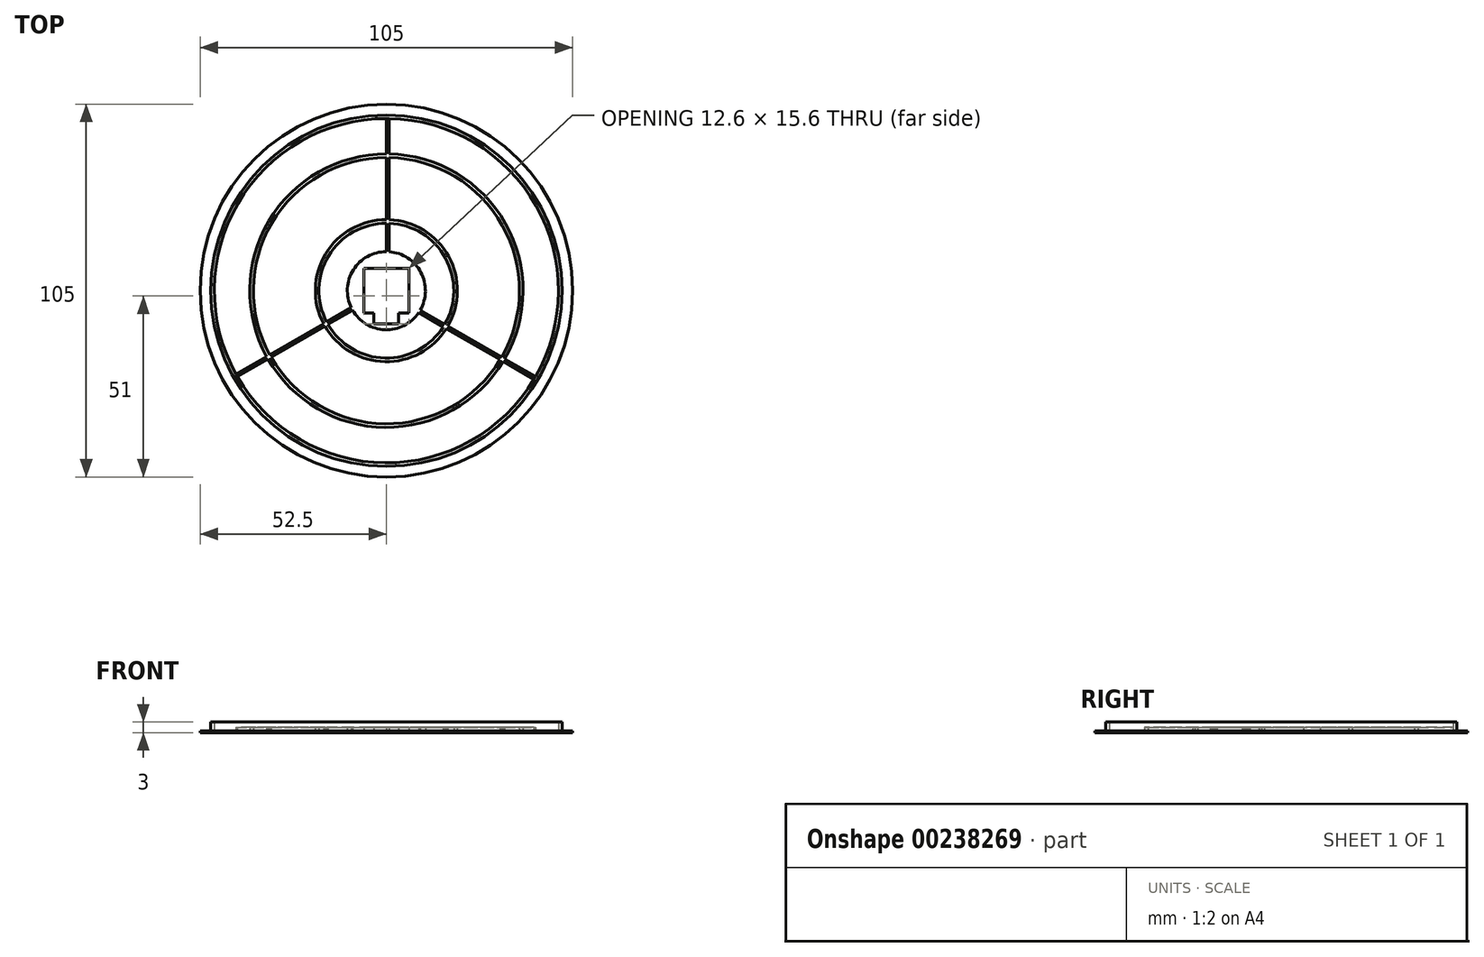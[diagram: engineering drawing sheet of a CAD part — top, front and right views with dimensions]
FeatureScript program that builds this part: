
annotation { "Feature Type Name" : "Feature", "Feature Type Description" : "" }
export const myFeature = defineFeature(function(context is Context, id is Id, definition is map)
    precondition{}
    {
        {
            var Q0;
            Q0=qCreatedBy(makeId("Top.planeOp"),FACE);
            var sketch = newSketch(context, id + "F0", { "sketchPlane" : qUnion([Q0])});
            skLineSegment(sketch, "E0.bottom", {"start": v(6.3, -6.3) * mm, "end": v(-6.3, -6.3) * mm});
            skLineSegment(sketch, "E0.top", {"start": v(6.3, 6.3) * mm, "end": v(-6.3, 6.3) * mm});
            skLineSegment(sketch, "E0.left", {"start": v(6.3, -6.3) * mm, "end": v(6.3, 6.3) * mm});
            skLineSegment(sketch, "E0.right", {"start": v(-6.3, -6.3) * mm, "end": v(-6.3, 6.3) * mm});
            skPoint(sketch, "E0.middle", {"position": v(0, 0) * mm});
            skCircle(sketch, "E1", {"center": v(0, 0) * mm, "radius": 11 * mm});
            skCircle(sketch, "E2", {"center": v(0, 0) * mm, "radius": 52.5 * mm});
            skLineSegment(sketch, "E3.bottom", {"start": v(3.5, -9.3) * mm, "end": v(-3.5, -9.3) * mm});
            skLineSegment(sketch, "E3.top", {"start": v(3.5, -6.3) * mm, "end": v(-3.5, -6.3) * mm});
            skLineSegment(sketch, "E3.left", {"start": v(3.5, -9.3) * mm, "end": v(3.5, -6.3) * mm});
            skLineSegment(sketch, "E3.right", {"start": v(-3.5, -9.3) * mm, "end": v(-3.5, -6.3) * mm});
            skPoint(sketch, "E3.middle", {"position": v(0, -7.8) * mm});
            skPoint(sketch, "E3.middle.positionSnap0", {"position": v(0, -6.3) * mm});
            skPoint(sketch, "E3.centerSnap0", {"position": v(0, -6.3) * mm});
            skCircle(sketch, "E4", {"center": v(0, 0) * mm, "radius": 49.5 * mm});
            skArc(sketch, "E5", {"start": v(0, 48.5) * mm, "mid": v(-41.8, 24.6) * mm, "end": v(-42.4, -23.56) * mm});
            skArc(sketch, "E6", {"start": v(-33.34, -19.25) * mm, "mid": v(-0.4, -38.5) * mm, "end": v(32.94, -19.93) * mm});
            skArc(sketch, "E7", {"start": v(-32.48, -18.75) * mm, "mid": v(-0.4, -37.5) * mm, "end": v(32.07, -19.43) * mm});
            skArc(sketch, "E8", {"start": v(-16.45, -9.5) * mm, "mid": v(-0.4, -19) * mm, "end": v(16.05, -10.18) * mm});
            skArc(sketch, "E9", {"start": v(-17.32, -10) * mm, "mid": v(-0.4, -20) * mm, "end": v(16.91, -10.68) * mm});
            skLineSegment(sketch, "E10", {"start": v(0, 11) * mm, "end": v(0, 19) * mm});
            skLineSegment(sketch, "E11", {"start": v(0.79, 48.5) * mm, "end": v(0.79, 38.5) * mm});
            skLineSegment(sketch, "E12.1.0", {"start": v(-9.53, -5.5) * mm, "end": v(-16.45, -9.5) * mm});
            skLineSegment(sketch, "E12.1.1", {"start": v(-42.4, -23.56) * mm, "end": v(-33.73, -18.56) * mm});
            skLineSegment(sketch, "E12.2.0", {"start": v(9.53, -5.5) * mm, "end": v(16.45, -9.5) * mm});
            skLineSegment(sketch, "E12.2.1", {"start": v(41.6, -24.93) * mm, "end": v(32.94, -19.93) * mm});
            skLineSegment(sketch, "E13.trimOffspring", {"start": v(-32.86, -18.06) * mm, "end": v(-17.7, -9.3) * mm});
            skLineSegment(sketch, "E14.trimOffspring", {"start": v(-33.34, -19.25) * mm, "end": v(-42, -24.25) * mm});
            skLineSegment(sketch, "E15.trimOffspring", {"start": v(-16.84, -8.8) * mm, "end": v(-9.9, -4.8) * mm});
            skLineSegment(sketch, "E16.trimOffspring", {"start": v(-17.32, -10) * mm, "end": v(-32.48, -18.75) * mm});
            skLineSegment(sketch, "E17.trimOffspring", {"start": v(16.05, -10.18) * mm, "end": v(9.1, -6.17) * mm});
            skArc(sketch, "E18.trimOffspring", {"start": v(16.45, -9.5) * mm, "mid": v(16.65, 9.16) * mm, "end": v(0.79, 18.98) * mm});
            skLineSegment(sketch, "E19.trimOffspring", {"start": v(17.32, -10) * mm, "end": v(32.48, -18.75) * mm});
            skArc(sketch, "E20.trimOffspring", {"start": v(17.32, -10) * mm, "mid": v(17.51, 9.66) * mm, "end": v(0.79, 19.98) * mm});
            skArc(sketch, "E21.trimOffspring", {"start": v(0, 20) * mm, "mid": v(-17.12, 10.34) * mm, "end": v(-17.7, -9.3) * mm});
            skLineSegment(sketch, "E22.trimOffspring", {"start": v(0, 20) * mm, "end": v(0, 37.5) * mm});
            skArc(sketch, "E23.trimOffspring", {"start": v(0, 19) * mm, "mid": v(-16.25, 9.84) * mm, "end": v(-16.84, -8.8) * mm});
            skLineSegment(sketch, "E24.trimOffspring", {"start": v(0.79, 18.98) * mm, "end": v(0.79, 10.97) * mm});
            skArc(sketch, "E25.trimOffspring", {"start": v(0, 38.5) * mm, "mid": v(-33.14, 19.6) * mm, "end": v(-33.73, -18.56) * mm});
            skLineSegment(sketch, "E26.trimOffspring", {"start": v(0, 38.5) * mm, "end": v(0, 48.5) * mm});
            skArc(sketch, "E27.trimOffspring", {"start": v(0, 37.5) * mm, "mid": v(-32.28, 19.1) * mm, "end": v(-32.86, -18.06) * mm});
            skLineSegment(sketch, "E28.trimOffspring", {"start": v(0.79, 37.5) * mm, "end": v(0.79, 19.98) * mm});
            skArc(sketch, "E29.trimOffspring", {"start": v(33.34, -19.25) * mm, "mid": v(33.54, 18.9) * mm, "end": v(0.79, 38.5) * mm});
            skArc(sketch, "E30.trimOffspring", {"start": v(32.48, -18.75) * mm, "mid": v(32.67, 18.4) * mm, "end": v(0.79, 37.5) * mm});
            skLineSegment(sketch, "E31.trimOffspring", {"start": v(32.07, -19.43) * mm, "end": v(16.91, -10.68) * mm});
            skLineSegment(sketch, "E32.trimOffspring", {"start": v(33.34, -19.25) * mm, "end": v(42, -24.25) * mm});
            skArc(sketch, "E33.trimOffspring", {"start": v(42, -24.25) * mm, "mid": v(42.2, 23.9) * mm, "end": v(0.79, 48.5) * mm});
            skArc(sketch, "E34.trimOffspring", {"start": v(-42, -24.25) * mm, "mid": v(-0.4, -48.5) * mm, "end": v(41.6, -24.93) * mm});
            skLineSegment(sketch, "E35", {"start": v(-42.4, -23.56) * mm, "end": v(-42, -24.25) * mm});
            skLineSegment(sketch, "E36", {"start": v(0, 48.5) * mm, "end": v(0.79, 48.5) * mm});
            skLineSegment(sketch, "E37", {"start": v(41.6, -24.93) * mm, "end": v(42, -24.25) * mm});
            skSolve(sketch);
        }
        {
            var Q0;
            Q0=makeQuery(id+"F0.imprint","IMPRINT",FACE,{"disambiguationData":[TD([[makeQuery(id+"F0.imprint","IMPRINT",EDGE,{"derivedFrom":sQuery(id+"F0.wireOp",EDGE,"E1")}),-1.0]])]});
            var Q1;
            Q1=makeQuery(id+"F0.imprint","IMPRINT",FACE,{"disambiguationData":[TD([[makeQuery(id+"F0.imprint","IMPRINT",EDGE,{"derivedFrom":sQuery(id+"F0.wireOp",EDGE,"E0.top")}),-1.0]])]});
            var Q2;
            Q2=makeQuery(id+"F0.imprint","IMPRINT",FACE,{"disambiguationData":[TD([[makeQuery(id+"F0.imprint","IMPRINT",EDGE,{"derivedFrom":sQuery(id+"F0.wireOp",EDGE,"E4")}),1.0]])]});
            var Q3;
            Q3=makeQuery(id+"F0.imprint","IMPRINT",FACE,{"disambiguationData":[TD([[makeQuery(id+"F0.imprint","IMPRINT",EDGE,{"derivedFrom":sQuery(id+"F0.wireOp",EDGE,"E2")}),1.0]])]});
            var Q4;
            Q4=makeQuery(id+"F0.imprint","IMPRINT",FACE,{"disambiguationData":[TD([[makeQuery(id+"F0.imprint","IMPRINT",EDGE,{"derivedFrom":sQuery(id+"F0.wireOp",EDGE,"E5")}),1.0]])]});
            var Q5;
            Q5=makeQuery(id+"F0.imprint","IMPRINT",FACE,{"disambiguationData":[TD([[makeQuery(id+"F0.imprint","IMPRINT",EDGE,{"derivedFrom":sQuery(id+"F0.wireOp",EDGE,"E6")}),1.0]])]});
            var Q6;
            Q6=makeQuery(id+"F0.imprint","IMPRINT",FACE,{"disambiguationData":[TD([[makeQuery(id+"F0.imprint","IMPRINT",EDGE,{"derivedFrom":sQuery(id+"F0.wireOp",EDGE,"E7")}),1.0]])]});
            var Q7;
            Q7=makeQuery(id+"F0.imprint","IMPRINT",FACE,{"disambiguationData":[TD([[makeQuery(id+"F0.imprint","IMPRINT",EDGE,{"derivedFrom":sQuery(id+"F0.wireOp",EDGE,"E8")}),-1.0]])]});
            var Q8;
            {var subQ0=sQuery(id+"F0.wireOp",EDGE,"E10");var subQ5=sQuery(id+"F0.wireOp",EDGE,"E6");var subQ6=makeQuery(id+"F0.imprint","INTERSECT",VERTEX,{"derivedFrom":[subQ5,subQ0]});Q8=makeQuery(id+"F0.imprint","IMPRINT",FACE,{"disambiguationData":[TD([[makeQuery(id+"F0.imprint","IMPRINT",EDGE,{"disambiguationData":[TD([[subQ6,-1.0]])],"derivedFrom":subQ5}),-1.0]])]});}
            var Q9;
            {var subQ0=sQuery(id+"F0.wireOp",EDGE,"E12.1.0");var subQ1=sQuery(id+"F0.wireOp",EDGE,"E5");var subQ2=makeQuery(id+"F0.imprint","INTERSECT",VERTEX,{"derivedFrom":[subQ1,subQ0]});Q9=makeQuery(id+"F0.imprint","IMPRINT",FACE,{"disambiguationData":[TD([[makeQuery(id+"F0.imprint","IMPRINT",EDGE,{"disambiguationData":[TD([[subQ2,-1.0]])],"derivedFrom":subQ1}),1.0]])]});}
            var Q10;
            {var subQ0=sQuery(id+"F0.wireOp",EDGE,"E11");var subQ5=sQuery(id+"F0.wireOp",EDGE,"E6");var subQ6=makeQuery(id+"F0.imprint","INTERSECT",VERTEX,{"derivedFrom":[subQ5,subQ0]});Q10=makeQuery(id+"F0.imprint","IMPRINT",FACE,{"disambiguationData":[TD([[makeQuery(id+"F0.imprint","IMPRINT",EDGE,{"disambiguationData":[TD([[subQ6,1.0]])],"derivedFrom":subQ5}),-1.0]])]});}
            var Q11;
            {var subQ0=sQuery(id+"F0.wireOp",EDGE,"E12.2.0");var subQ1=sQuery(id+"F0.wireOp",EDGE,"E5");var subQ2=makeQuery(id+"F0.imprint","INTERSECT",VERTEX,{"derivedFrom":[subQ1,subQ0]});Q11=makeQuery(id+"F0.imprint","IMPRINT",FACE,{"disambiguationData":[TD([[makeQuery(id+"F0.imprint","IMPRINT",EDGE,{"disambiguationData":[TD([[subQ2,1.0]])],"derivedFrom":subQ1}),1.0]])]});}
            var Q12;
            {var subQ0=sQuery(id+"F0.wireOp",EDGE,"E12.1.0");var subQ1=sQuery(id+"F0.wireOp",EDGE,"E5");var subQ2=makeQuery(id+"F0.imprint","INTERSECT",VERTEX,{"derivedFrom":[subQ1,subQ0]});Q12=makeQuery(id+"F0.imprint","IMPRINT",FACE,{"disambiguationData":[TD([[makeQuery(id+"F0.imprint","IMPRINT",EDGE,{"disambiguationData":[TD([[subQ2,1.0]])],"derivedFrom":subQ1}),1.0]])]});}
            var Q13;
            Q13=makeQuery(id+"F0.imprint","IMPRINT",FACE,{"disambiguationData":[TD([[makeQuery(id+"F0.imprint","IMPRINT",EDGE,{"derivedFrom":sQuery(id+"F0.wireOp",EDGE,"E13.trimOffspring")}),1.0]])]});
            var Q14;
            {var subQ0=sQuery(id+"F0.wireOp",EDGE,"E10");Q14=makeQuery(id+"F0.imprint","IMPRINT",FACE,{"disambiguationData":[TD([[makeQuery(id+"F0.imprint","IMPRINT",EDGE,{"derivedFrom":subQ0}),1.0]])]});}
            var Q15;
            {var subQ0=sQuery(id+"F0.wireOp",EDGE,"E12.2.0");Q15=makeQuery(id+"F0.imprint","IMPRINT",FACE,{"disambiguationData":[TD([[makeQuery(id+"F0.imprint","IMPRINT",EDGE,{"derivedFrom":subQ0}),1.0]])]});}
            var Q16;
            Q16=makeQuery(id+"F0.imprint","IMPRINT",FACE,{"disambiguationData":[TD([[makeQuery(id+"F0.imprint","IMPRINT",EDGE,{"derivedFrom":sQuery(id+"F0.wireOp",EDGE,"E8")}),1.0]])]});
            var Q17;
            Q17=makeQuery(id+"F0.imprint","IMPRINT",FACE,{"disambiguationData":[TD([[makeQuery(id+"F0.imprint","IMPRINT",EDGE,{"derivedFrom":sQuery(id+"F0.wireOp",EDGE,"E19.trimOffspring")}),1.0]])]});
            var Q18;
            Q18=makeQuery(id+"F0.imprint","IMPRINT",FACE,{"disambiguationData":[TD([[makeQuery(id+"F0.imprint","IMPRINT",EDGE,{"derivedFrom":sQuery(id+"F0.wireOp",EDGE,"E11")}),1.0]])]});
            extrude(context, id + "F1", {"entities" : qUnion([Q0, Q1, Q2, Q3, Q4, Q5, Q6, Q7, Q8, Q9, Q10, Q11, Q12, Q13, Q14, Q15, Q16, Q17, Q18]), "depth" : 0.5 * mm});
        }
        {
            var Q0;
            Q0=makeQuery(id+"F0.imprint","IMPRINT",FACE,{"disambiguationData":[TD([[makeQuery(id+"F0.imprint","IMPRINT",EDGE,{"derivedFrom":sQuery(id+"F0.wireOp",EDGE,"E4")}),1.0]])]});
            extrude(context, id + "F2", {"entities" : qUnion([Q0]), "operationType" : NewBodyOperationType.ADD, "depth" : 3 * mm});
        }
        {
            var Q0;
            Q0=makeQuery(id+"F0.imprint","IMPRINT",FACE,{"disambiguationData":[TD([[makeQuery(id+"F0.imprint","IMPRINT",EDGE,{"derivedFrom":sQuery(id+"F0.wireOp",EDGE,"E6")}),1.0]])]});
            var Q1;
            Q1=makeQuery(id+"F0.imprint","IMPRINT",FACE,{"disambiguationData":[TD([[makeQuery(id+"F0.imprint","IMPRINT",EDGE,{"derivedFrom":sQuery(id+"F0.wireOp",EDGE,"E0.top")}),-1.0]])]});
            extrude(context, id + "F3", {"entities" : qUnion([Q0, Q1]), "operationType" : NewBodyOperationType.ADD, "depth" : 1.5 * mm});
        }
    });
